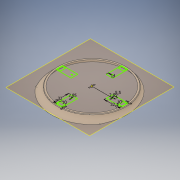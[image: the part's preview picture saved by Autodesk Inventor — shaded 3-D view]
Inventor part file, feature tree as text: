
AUTODESK INVENTOR PART (.ipt)
format: ipt  version: 2019.4 (Build 234330000, 330)  size: 925,184 bytes
history: native  units: mm
features: sketch x13, extrude x10, hole x8, plane x7, delete_face x4, fillet x3, revolve x1, loft x1, other x1
ambient origin geometry x8: Origin, YZ Plane, XZ Plane, XY Plane, X Axis, Y Axis, Z Axis, Center Point
bodies: Solid1 (feature_tree)
feature tree (48):
  revolve  "Revolution1"  [1 undecoded]
  extrude  "Extrusion2"  Depth=94.0mm
  plane  "Work Plane1"
  sketch  "Sketch5"  dims[d10=0.0mm d12=180.0deg]
  plane  "Work Plane2"
  plane  "Work Plane6"
  sketch  "Sketch8"  dims[d23=3.0mm d24=170.0mm d25=0.0mm]
  loft  "Loft2"
  extrude  "Extrusion4"  Depth=50.0mm
  delete_face  "Delete Face1"
  delete_face  "Delete Face2"
  sketch  "Sketch10"  dims[d27=90.0mm d28=85.0mm]
  hole  "Hole1"  [1 undecoded]
  hole  "Hole2"  [1 undecoded]
  hole  "Hole3"  [1 undecoded]
  hole  "Hole4"  [1 undecoded]
  hole  "Hole5"  [1 undecoded]
  hole  "Hole6"  [1 undecoded]
  hole  "Hole7"  [1 undecoded]
  hole  "Hole8"  [1 undecoded]
  plane  "Work Plane7"
  extrude  "Extrusion5"  Depth=10.0mm
  fillet  "Fillet4"  Radius=15.0mm
  fillet  "Fillet5"  Radius=17.0mm
  fillet  "Fillet6"  Radius=9.0mm
  plane  "Work Plane8"
  extrude  "Extrusion7"  Depth=10.0mm
  plane  "Work Plane9"
  sketch  "Sketch15"  dims[d45=83.0mm d46=41.5mm]
  extrude  "Extrusion8"  Depth=10.0mm
  extrude  "Extrusion9"  Depth=10.0mm
  extrude  "Extrusion10"  Depth=10.0mm
  extrude  "Extrusion11"  Depth=10.0mm
  plane  "Work Plane10"
  extrude  "Extrusion12"  Depth=10.0mm
  extrude  "Extrusion13"  Depth=10.0mm
  delete_face  "Delete Face3"
  delete_face  "Delete Face4"
  sketch  "Sketch2"  dims[d3=5.0mm d4=1.5mm]
  sketch  "Sketch4"  dims[d5=80.0mm d8=94.0mm]
  other  "Edges2"
  sketch  "Sketch11"  dims[d29=57.0mm d30=28.5mm]
  sketch  "Sketch13"  dims[d31=42.5mm d32=-10.0mm d37=9.0mm]
  sketch  "Sketch16"  dims[d49=55.0mm d50=27.5mm]
  sketch  "Sketch17"  dims[d51=5.0mm d53=5.0mm]
  sketch  "Sketch18"  dims[d54=5.0mm d55=5.0mm]
  sketch  "Sketch19"  dims[d56=9.0mm d58=8.0mm d59=15.0mm d60=15.0mm d61=17.0mm d62=9.0mm d63=17.0mm d64=18.0mm d65=8.0mm d66=6.0mm d67=6.0mm d68=6.0mm d69=8.0mm d70=9.0mm d71=6.0mm d91=85.0mm d92=57.0mm d93=28.5mm d94=83.0mm d95=55.0mm d96=5.0mm d97=5.0mm d98=5.0mm d99=5.0mm d100=9.0mm d101=8.0mm d102=9.0mm d103=8.0mm d104=6.0mm d105=6.0mm d106=6.0mm d107=8.0mm d108=9.0mm d109=6.0mm d110=0.0mm d111=90.0deg d112=0.0mm d113=90.0deg d114=0.0mm d115=90.0deg d118=10.0mm d119=0.0mm d120=5.0mm d121=0.0mm d122=151.0mm d124=8.0mm d125=6.0mm d126=4.0mm d127=2.0mm d128=90.0deg d129=8.0mm d130=20.594885mm d131=8.0mm d132=6.0mm d133=4.0mm d134=2.0mm d135=90.0deg d136=8.0mm d137=20.594885mm d138=5.0mm d139=6.0mm d140=4.0mm d141=2.0mm d142=90.0deg d143=8.0mm d144=20.594885mm d145=5.0mm d146=6.0mm d147=4.0mm d148=2.0mm d149=90.0deg d150=8.0mm d151=20.594885mm d152=5.0mm d153=6.0mm d154=4.0mm d155=2.0mm d156=90.0deg d157=8.0mm d158=20.594885mm d159=5.0mm d160=6.0mm d161=4.0mm d162=2.0mm d163=90.0deg d164=8.0mm d165=20.594885mm d166=8.0mm d167=6.0mm d168=4.0mm d169=2.0mm d170=90.0deg d171=8.0mm d172=20.594885mm d173=151.0mm d174=30.683mm d175=3.023mm d176=2.0mm d177=14.3117mm d178=0.1mm d179=12.391838mm d180=86.25mm d181=26.0mm d182=13.0mm d183=13.0mm d184=16.0mm d185=16.0mm d186=30.0mm d187=170.0mm d188=0.0mm d189=2.0mm d190=2.0mm d191=2.0mm d192=10.0mm d193=2.85mm d203=10.0mm d204=7.0mm d208=1.0mm d209=32.0mm d210=14.0mm d220=2.0mm d221=0.0mm d222=46.0mm d236=2.0mm d237=0.0mm d238=5.0mm d239=41.509691mm d240=2.5mm d241=40.0mm d242=10.0mm d243=25.0mm d244=0.0mm d245=17.5mm d246=3.0mm d247=3.0mm d248=3.0mm d249=3.0mm d250=19.0mm d251=24.0mm d252=0.0mm d253=0.0mm d254=44.0mm d255=44.0mm d256=22.0mm d257=22.0mm d258=31.25mm d259=0.0mm d260=-79.5mm d261=12.0mm d262=55.0mm d263=51.5mm d264=0.0mm d265=2.85mm d266=10.0mm d267=7.0mm d268=1.0mm d269=32.0mm d275=0.0mm d276=7.0mm d277=83.75mm d278=0.0mm d279=5.5mm]
  sketch  "Sketch6"  dims[d15=0.0mm d22=50.0mm]
note: 9 required parameter values undecoded (feature->parameter linkage not recoverable at this tier; creation-order binding heuristic only, values carry confidence <= 0.55)